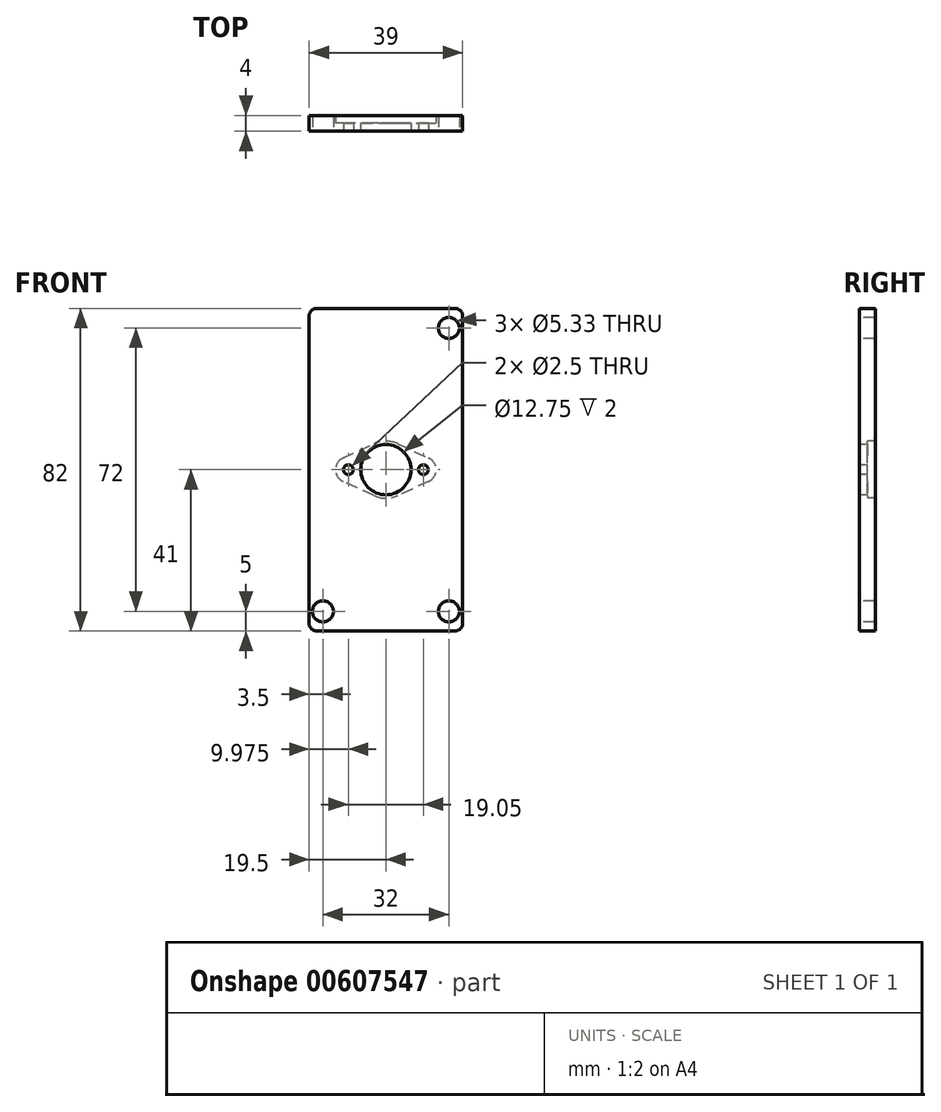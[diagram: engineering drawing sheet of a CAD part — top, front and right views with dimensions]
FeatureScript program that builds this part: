
annotation { "Feature Type Name" : "Feature", "Feature Type Description" : "" }
export const myFeature = defineFeature(function(context is Context, id is Id, definition is map)
    precondition{}
    {
        {
            var Q0;
            Q0=qCreatedBy(makeId("Front.planeOp"),FACE);
            var sketch = newSketch(context, id + "F0", { "sketchPlane" : qUnion([Q0])});
            skLineSegment(sketch, "E0.bottom", {"start": v(17.5, 41) * mm, "end": v(-17.5, 41) * mm});
            skLineSegment(sketch, "E0.top", {"start": v(17.5, -41) * mm, "end": v(-17.5, -41) * mm});
            skLineSegment(sketch, "E0.left", {"start": v(19.5, 39) * mm, "end": v(19.5, -39) * mm});
            skLineSegment(sketch, "E0.right", {"start": v(-19.5, 39) * mm, "end": v(-19.5, -39) * mm});
            skPoint(sketch, "E0.middle", {"position": v(0, 0) * mm});
            skLineSegment(sketch, "E1", {"start": v(-16, -36) * mm, "end": v(16, -36) * mm, "construction": true});
            skPoint(sketch, "E2", {"position": v(0, -36) * mm});
            skCircle(sketch, "E3", {"center": v(-16, -36) * mm, "radius": 2.67 * mm});
            skCircle(sketch, "E4", {"center": v(16, -36) * mm, "radius": 2.67 * mm});
            skLineSegment(sketch, "E5", {"start": v(16, -36) * mm, "end": v(16, 36) * mm, "construction": true});
            skCircle(sketch, "E6", {"center": v(16, 36) * mm, "radius": 2.67 * mm});
            skPoint(sketch, "E7", {"position": v(16, 0) * mm});
            skCircle(sketch, "E8", {"center": v(0, 0) * mm, "radius": 6.38 * mm});
            skCircle(sketch, "E9", {"center": v(-9.53, 0) * mm, "radius": 1.25 * mm});
            skCircle(sketch, "E10", {"center": v(9.53, 0) * mm, "radius": 1.25 * mm});
            skPoint(sketch, "E11.visualSharp", {"position": v(-19.5, 41) * mm});
            skArc(sketch, "E11.filletArc", {"start": v(-17.5, 41) * mm, "mid": v(-18.91, 40.41) * mm, "end": v(-19.5, 39) * mm});
            skPoint(sketch, "E12.visualSharp", {"position": v(19.5, 41) * mm});
            skArc(sketch, "E12.filletArc", {"start": v(19.5, 39) * mm, "mid": v(18.91, 40.41) * mm, "end": v(17.5, 41) * mm});
            skPoint(sketch, "E13.visualSharp", {"position": v(19.5, -41) * mm});
            skArc(sketch, "E13.filletArc", {"start": v(17.5, -41) * mm, "mid": v(18.91, -40.41) * mm, "end": v(19.5, -39) * mm});
            skPoint(sketch, "E14.visualSharp", {"position": v(-19.5, -41) * mm});
            skArc(sketch, "E14.filletArc", {"start": v(-19.5, -39) * mm, "mid": v(-18.91, -40.41) * mm, "end": v(-17.5, -41) * mm});
            skCircle(sketch, "E15", {"center": v(0, 0) * mm, "radius": 7.25 * mm});
            skCircle(sketch, "E16", {"center": v(9.53, 0) * mm, "radius": 3.25 * mm});
            skCircle(sketch, "E17", {"center": v(-9.53, 0) * mm, "radius": 3.25 * mm});
            skLineSegment(sketch, "E18", {"start": v(-10.89, 2.95) * mm, "end": v(-3.04, 6.58) * mm});
            skLineSegment(sketch, "E19", {"start": v(3.04, 6.58) * mm, "end": v(10.89, 2.95) * mm});
            skLineSegment(sketch, "E20", {"start": v(10.89, -2.95) * mm, "end": v(3.04, -6.58) * mm});
            skLineSegment(sketch, "E21", {"start": v(-3.04, -6.58) * mm, "end": v(-10.89, -2.95) * mm});
            skSolve(sketch);
        }
        {
            var Q0;
            Q0=makeQuery(id+"F0.imprint","IMPRINT",FACE,{"disambiguationData":[TD([[makeQuery(id+"F0.imprint","IMPRINT",EDGE,{"derivedFrom":sQuery(id+"F0.wireOp",EDGE,"E0.bottom")}),1.0]])]});
            extrude(context, id + "F1", {"entities" : qUnion([Q0]), "oppositeDirection" : true, "depth" : 4 * mm, "offsetDistance" : 25 * mm});
        }
        {
            var Q0;
            Q0=makeQuery(id+"F0.imprint","IMPRINT",FACE,{"disambiguationData":[TD([[makeQuery(id+"F0.imprint","IMPRINT",EDGE,{"derivedFrom":sQuery(id+"F0.wireOp",EDGE,"E9")}),-1.0]])]});
            var Q1;
            {var subQ0=sQuery(id+"F0.wireOp",EDGE,"E18");Q1=makeQuery(id+"F0.imprint","IMPRINT",FACE,{"disambiguationData":[TD([[makeQuery(id+"F0.imprint","IMPRINT",EDGE,{"derivedFrom":subQ0}),-1.0]])]});}
            var Q2;
            {var subQ0=sQuery(id+"F0.wireOp",EDGE,"E21");Q2=makeQuery(id+"F0.imprint","IMPRINT",FACE,{"disambiguationData":[TD([[makeQuery(id+"F0.imprint","IMPRINT",EDGE,{"derivedFrom":subQ0}),-1.0]])]});}
            var Q3;
            {var subQ5=sQuery(id+"F0.wireOp",EDGE,"E17");var subQ7=sQuery(id+"F0.wireOp",EDGE,"E8");var subQ8=makeQuery(id+"F0.imprint","INTERSECT",VERTEX,{"disambiguationData":[OD(1.0)],"derivedFrom":[subQ7,subQ5]});Q3=makeQuery(id+"F0.imprint","IMPRINT",FACE,{"disambiguationData":[TD([[makeQuery(id+"F0.imprint","IMPRINT",EDGE,{"disambiguationData":[TD([[subQ8,-1.0]])],"derivedFrom":subQ7}),-1.0]])]});}
            var Q4;
            {var subQ0=sQuery(id+"F0.wireOp",EDGE,"E17");var subQ1=sQuery(id+"F0.wireOp",EDGE,"E8");var subQ2=makeQuery(id+"F0.imprint","INTERSECT",VERTEX,{"disambiguationData":[OD(0.0)],"derivedFrom":[subQ1,subQ0]});Q4=makeQuery(id+"F0.imprint","IMPRINT",FACE,{"disambiguationData":[TD([[makeQuery(id+"F0.imprint","IMPRINT",EDGE,{"disambiguationData":[TD([[subQ2,-1.0]])],"derivedFrom":subQ1}),-1.0]])]});}
            var Q5;
            {var subQ2=sQuery(id+"F0.wireOp",EDGE,"E17");var subQ5=sQuery(id+"F0.wireOp",EDGE,"E8");var subQ6=makeQuery(id+"F0.imprint","INTERSECT",VERTEX,{"disambiguationData":[OD(0.0)],"derivedFrom":[subQ5,subQ2]});Q5=makeQuery(id+"F0.imprint","IMPRINT",FACE,{"disambiguationData":[TD([[makeQuery(id+"F0.imprint","IMPRINT",EDGE,{"disambiguationData":[TD([[subQ6,1.0]])],"derivedFrom":subQ5}),-1.0]])]});}
            var Q6;
            {var subQ0=sQuery(id+"F0.wireOp",EDGE,"E16");var subQ1=sQuery(id+"F0.wireOp",EDGE,"E8");var subQ2=makeQuery(id+"F0.imprint","INTERSECT",VERTEX,{"disambiguationData":[OD(0.0)],"derivedFrom":[subQ1,subQ0]});Q6=makeQuery(id+"F0.imprint","IMPRINT",FACE,{"disambiguationData":[TD([[makeQuery(id+"F0.imprint","IMPRINT",EDGE,{"disambiguationData":[TD([[subQ2,1.0]])],"derivedFrom":subQ1}),-1.0]])]});}
            var Q7;
            Q7=makeQuery(id+"F0.imprint","IMPRINT",FACE,{"disambiguationData":[TD([[makeQuery(id+"F0.imprint","IMPRINT",EDGE,{"derivedFrom":sQuery(id+"F0.wireOp",EDGE,"E10")}),-1.0]])]});
            var Q8;
            {var subQ0=sQuery(id+"F0.wireOp",EDGE,"E20");Q8=makeQuery(id+"F0.imprint","IMPRINT",FACE,{"disambiguationData":[TD([[makeQuery(id+"F0.imprint","IMPRINT",EDGE,{"derivedFrom":subQ0}),-1.0]])]});}
            var Q9;
            {var subQ0=sQuery(id+"F0.wireOp",EDGE,"E19");Q9=makeQuery(id+"F0.imprint","IMPRINT",FACE,{"disambiguationData":[TD([[makeQuery(id+"F0.imprint","IMPRINT",EDGE,{"derivedFrom":subQ0}),-1.0]])]});}
            extrude(context, id + "F2", {"entities" : qUnion([Q0, Q1, Q2, Q3, Q4, Q5, Q6, Q7, Q8, Q9]), "operationType" : NewBodyOperationType.ADD, "oppositeDirection" : true, "depth" : 2 * mm, "offsetDistance" : 25 * mm});
        }
    });
